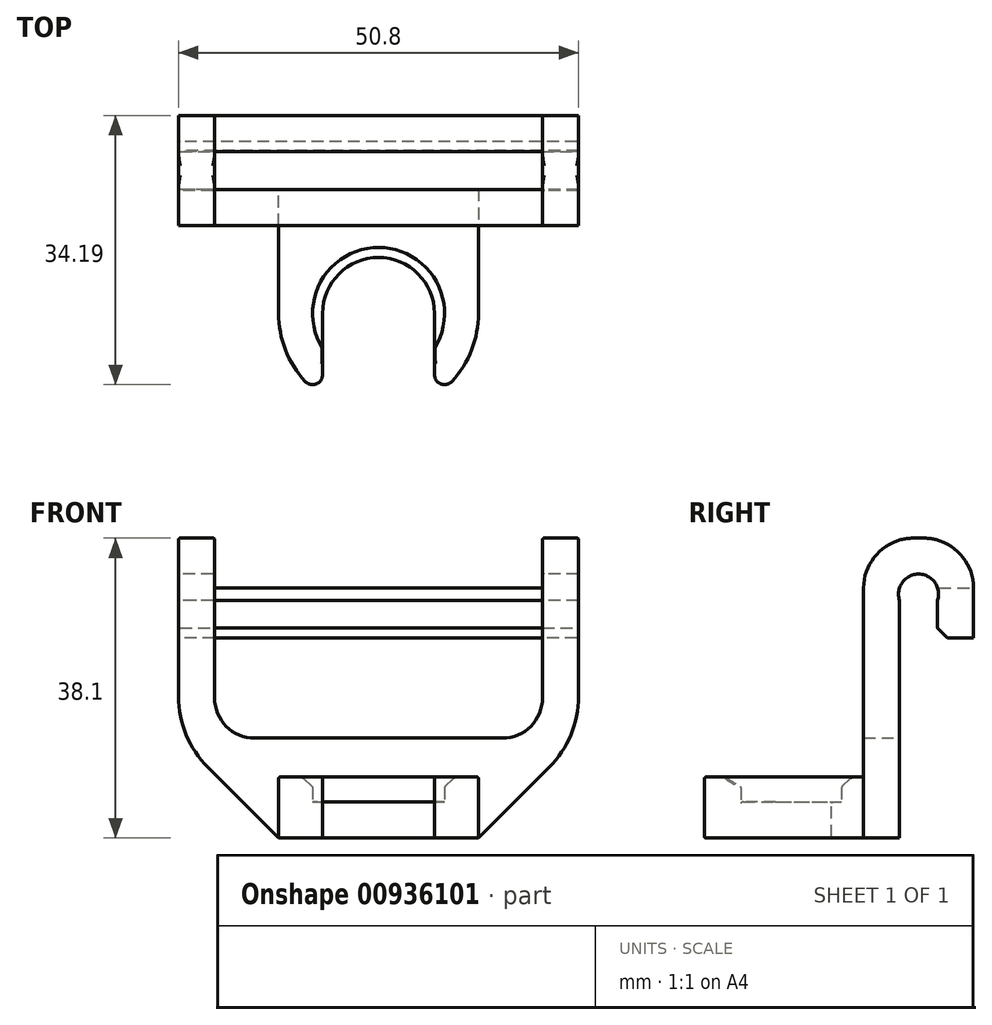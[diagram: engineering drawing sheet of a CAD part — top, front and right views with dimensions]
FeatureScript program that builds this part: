
annotation { "Feature Type Name" : "Feature", "Feature Type Description" : "" }
export const myFeature = defineFeature(function(context is Context, id is Id, definition is map)
    precondition{}
    {
        {
            var Q0;
            Q0=qCreatedBy(makeId("Top.planeOp"),FACE);
            var sketch = newSketch(context, id + "F0", { "sketchPlane" : qUnion([Q0])});
            skArc(sketch, "E0", {"start": v(-12.7, 0) * mm, "mid": v(0, -12.7) * mm, "end": v(12.7, 0) * mm});
            skLineSegment(sketch, "E1.top", {"start": v(-12.7, 11.18) * mm, "end": v(12.7, 11.18) * mm});
            skLineSegment(sketch, "E1.left", {"start": v(-12.7, 0) * mm, "end": v(-12.7, 11.18) * mm});
            skLineSegment(sketch, "E1.right", {"start": v(12.7, 0) * mm, "end": v(12.7, 11.18) * mm});
            skLineSegment(sketch, "E2", {"start": v(-12.7, 0) * mm, "end": v(12.7, 0) * mm, "construction": true});
            skSolve(sketch);
        }
        {
            var Q0;
            Q0=makeQuery(id+"F0.imprint","IMPRINT",FACE,{"disambiguationData":[TD([[makeQuery(id+"F0.imprint","IMPRINT",EDGE,{"derivedFrom":sQuery(id+"F0.wireOp",EDGE,"E0")}),1.0]])]});
            extrude(context, id + "F1", {"entities" : qUnion([Q0]), "depth" : 4.57 * mm, "offsetDistance" : 25.4 * mm});
        }
        {
            var Q0;
            Q0=makeQuery(id+"F1.opExtrude","CAP_FACE",FACE,{"disambiguationData":[OSD([sQuery(id+"F0.wireOp",EDGE,"E0"),sQuery(id+"F0.wireOp",EDGE,"E1.top"),sQuery(id+"F0.wireOp",EDGE,"E1.left"),sQuery(id+"F0.wireOp",EDGE,"E1.right")])],"isStart":false});
            var sketch = newSketch(context, id + "F2", { "sketchPlane" : qUnion([Q0])});
            skCircle(sketch, "E3", {"center": v(0, 0) * mm, "radius": 8.38 * mm});
            skArc(sketch, "E4", {"start": v(-12.7, 0) * mm, "mid": v(0, -12.7) * mm, "end": v(12.7, 0) * mm});
            skLineSegment(sketch, "E5.bottom", {"start": v(-12.7, 11.18) * mm, "end": v(12.7, 11.18) * mm});
            skLineSegment(sketch, "E5.left", {"start": v(-12.7, 11.18) * mm, "end": v(-12.7, 0) * mm});
            skLineSegment(sketch, "E5.right", {"start": v(12.7, 11.18) * mm, "end": v(12.7, 0) * mm});
            skSolve(sketch);
        }
        {
            var Q0;
            Q0 = qSketchRegion(id + "F2", true);
            extrude(context, id + "F3", {"entities" : qUnion([Q0]), "operationType" : NewBodyOperationType.ADD, "depth" : 3.17 * mm, "offsetDistance" : 25.4 * mm});
        }
        {
            var Q0;
            Q0=makeQuery(id+"F1.opExtrude","CAP_FACE",FACE,{"disambiguationData":[OSD([sQuery(id+"F0.wireOp",EDGE,"E0"),sQuery(id+"F0.wireOp",EDGE,"E1.top"),sQuery(id+"F0.wireOp",EDGE,"E1.left"),sQuery(id+"F0.wireOp",EDGE,"E1.right")])],"isStart":false});
            var sketch = newSketch(context, id + "F4", { "sketchPlane" : qUnion([Q0])});
            skArc(sketch, "E6", {"start": v(7.11, 0) * mm, "mid": v(0, 7.11) * mm, "end": v(-7.11, 0) * mm});
            skLineSegment(sketch, "E7.top", {"start": v(-7.11, -29.61) * mm, "end": v(7.11, -29.61) * mm});
            skLineSegment(sketch, "E7.left", {"start": v(-7.11, 0) * mm, "end": v(-7.11, -29.61) * mm});
            skLineSegment(sketch, "E7.right", {"start": v(7.11, 0) * mm, "end": v(7.11, -29.61) * mm});
            skLineSegment(sketch, "E8", {"start": v(-7.11, 0) * mm, "end": v(7.11, 0) * mm, "construction": true});
            skSolve(sketch);
        }
        {
            var Q0;
            Q0 = qSketchRegion(id + "F4", true);
            extrude(context, id + "F5", {"entities" : qUnion([Q0]), "operationType" : NewBodyOperationType.REMOVE, "oppositeDirection" : true, "depth" : 25.4 * mm, "offsetDistance" : 25.4 * mm, "symmetric" : true});
        }
        {
            var Q0;
            Q0=makeQuery(id+"F5.boolean.opBoolean","INTERSECT",EDGE,{"derivedFrom":[makeQuery(id+"F3.boolean.opBoolean","MERGE",FACE,{"derivedFrom":[makeQuery(id+"F1.opExtrude","SWEPT_FACE",FACE,{"disambiguationData":[OSD([sQuery(id+"F0.wireOp",EDGE,"E0")])]}),makeQuery(id+"F3.opExtrude","SWEPT_FACE",FACE,{"disambiguationData":[OSD([sQuery(id+"F2.wireOp",EDGE,"E4")])]})]}),makeQuery(id+"F5.opExtrude","SWEPT_FACE",FACE,{"disambiguationData":[OSD([sQuery(id+"F4.wireOp",EDGE,"E7.left")])]})]});
            var Q1;
            Q1=makeQuery(id+"F5.boolean.opBoolean","INTERSECT",EDGE,{"derivedFrom":[makeQuery(id+"F3.boolean.opBoolean","MERGE",FACE,{"derivedFrom":[makeQuery(id+"F1.opExtrude","SWEPT_FACE",FACE,{"disambiguationData":[OSD([sQuery(id+"F0.wireOp",EDGE,"E0")])]}),makeQuery(id+"F3.opExtrude","SWEPT_FACE",FACE,{"disambiguationData":[OSD([sQuery(id+"F2.wireOp",EDGE,"E4")])]})]}),makeQuery(id+"F5.opExtrude","SWEPT_FACE",FACE,{"disambiguationData":[OSD([sQuery(id+"F4.wireOp",EDGE,"E7.right")])]})]});
            fillet(context, id + "F6", {"entities" : qUnion([Q0, Q1]), "radius" : 1.27 * mm, "tangentPropagation" : true, "allowEdgeOverflow" : false});
        }
        {
            var Q0;
            Q0=makeQuery(id+"F3.opExtrude","CAP_EDGE",EDGE,{"disambiguationData":[OSD([sQuery(id+"F2.wireOp",EDGE,"E3")])],"isStart":false});
            chamfer(context, id + "F7", {"entities" : qUnion([Q0]), "width" : 1.27 * mm});
        }
        {
            var Q0;
            Q0=qCreatedBy(makeId("Right.planeOp"),FACE);
            var sketch = newSketch(context, id + "F8", { "sketchPlane" : qUnion([Q0])});
            skLineSegment(sketch, "E9.bottom", {"start": v(25.15, 0) * mm, "end": v(11.18, 0) * mm});
            skLineSegment(sketch, "E9.top", {"start": v(25.15, 38.1) * mm, "end": v(11.18, 38.1) * mm});
            skLineSegment(sketch, "E9.left", {"start": v(11.18, 0) * mm, "end": v(11.18, 38.1) * mm});
            skLineSegment(sketch, "E9.right", {"start": v(25.15, 0) * mm, "end": v(25.15, 38.1) * mm});
            skSolve(sketch);
        }
        {
            var Q0;
            Q0 = qSketchRegion(id + "F8", true);
            extrude(context, id + "F9", {"entities" : qUnion([Q0]), "operationType" : NewBodyOperationType.ADD, "depth" : 50.8 * mm, "offsetDistance" : 25.4 * mm, "symmetric" : true});
        }
        {
            var Q0;
            Q0=makeQuery(id+"F9.opExtrude","CAP_EDGE",EDGE,{"disambiguationData":[OSD([sQuery(id+"F8.wireOp",EDGE,"E9.bottom")])],"isStart":false});
            var Q1;
            Q1=makeQuery(id+"F9.opExtrude","CAP_EDGE",EDGE,{"disambiguationData":[OSD([sQuery(id+"F8.wireOp",EDGE,"E9.bottom")])],"isStart":true});
            chamfer(context, id + "F10", {"entities" : qUnion([Q0, Q1]), "width" : 12.7 * mm, "tangentPropagation" : true});
        }
        {
            var Q0;
            Q0=makeQuery(id+"F9.opExtrude","CAP_FACE",FACE,{"disambiguationData":[OSD([sQuery(id+"F8.wireOp",EDGE,"E9.bottom"),sQuery(id+"F8.wireOp",EDGE,"E9.top"),sQuery(id+"F8.wireOp",EDGE,"E9.left"),sQuery(id+"F8.wireOp",EDGE,"E9.right")])],"isStart":true});
            var sketch = newSketch(context, id + "F11", { "sketchPlane" : qUnion([Q0])});
            skLineSegment(sketch, "E10", {"start": v(-18.16, 38.1) * mm, "end": v(-18.16, 12.7) * mm, "construction": true});
            skArc(sketch, "E11", {"start": v(-15.75, 30.2) * mm, "mid": v(-18.16, 33.53) * mm, "end": v(-20.57, 30.2) * mm});
            skPoint(sketch, "E12", {"position": v(-18.16, 33.53) * mm});
            skLineSegment(sketch, "E13.left", {"start": v(-20.57, 30.2) * mm, "end": v(-20.57, 25.4) * mm});
            skLineSegment(sketch, "E13.right", {"start": v(-15.75, 30.2) * mm, "end": v(-15.75, 0) * mm});
            skPoint(sketch, "E13.middle", {"position": v(-18.16, 15.1) * mm});
            skLineSegment(sketch, "E14.bottom", {"start": v(-20.57, 25.4) * mm, "end": v(-25.15, 25.4) * mm});
            skLineSegment(sketch, "E14.top", {"start": v(-15.75, 0) * mm, "end": v(-25.15, 0) * mm});
            skLineSegment(sketch, "E14.right", {"start": v(-25.15, 25.4) * mm, "end": v(-25.15, 0) * mm});
            skPoint(sketch, "E13.top.start.orphan", {"position": v(-20.57, 0) * mm});
            skSolve(sketch);
        }
        {
            var Q0;
            Q0 = qSketchRegion(id + "F11", true);
            var Q1;
            Q1=makeQuery(id+"F9.opExtrude","CAP_FACE",FACE,{"disambiguationData":[OSD([sQuery(id+"F8.wireOp",EDGE,"E9.bottom"),sQuery(id+"F8.wireOp",EDGE,"E9.top"),sQuery(id+"F8.wireOp",EDGE,"E9.left"),sQuery(id+"F8.wireOp",EDGE,"E9.right")])],"isStart":false});
            extrude(context, id + "F12", {"entities" : qUnion([Q0]), "operationType" : NewBodyOperationType.REMOVE, "endBound" : BoundingType.UP_TO_SURFACE, "oppositeDirection" : true, "depth" : 25.4 * mm, "endBoundEntityFace" : qUnion([Q1]), "offsetDistance" : 25.4 * mm});
        }
        {
            var Q0;
            Q0=makeQuery(id+"F12.boolean.opBoolean","COPY",EDGE,{"derivedFrom":makeQuery(id+"F12.opExtrude","SWEPT_EDGE",EDGE,{"disambiguationData":[OSD([sQuery(id+"F11.wireOp",EDGE,"E13.left"),sQuery(id+"F11.wireOp",EDGE,"E14.bottom")])]})});
            chamfer(context, id + "F13", {"entities" : qUnion([Q0]), "width" : 1.27 * mm, "tangentPropagation" : true});
        }
        {
            var Q0;
            Q0=makeQuery(id+"F9.opExtrude","SWEPT_EDGE",EDGE,{"disambiguationData":[OSD([sQuery(id+"F8.wireOp",EDGE,"E9.top"),sQuery(id+"F8.wireOp",EDGE,"E9.left")])]});
            var Q1;
            Q1=makeQuery(id+"F9.opExtrude","SWEPT_EDGE",EDGE,{"disambiguationData":[OSD([sQuery(id+"F8.wireOp",EDGE,"E9.top"),sQuery(id+"F8.wireOp",EDGE,"E9.right")])]});
            fillet(context, id + "F14", {"entities" : qUnion([Q0, Q1]), "radius" : 6.35 * mm, "tangentPropagation" : true, "allowEdgeOverflow" : false});
        }
        {
            var Q0;
            {var subQ0=sQuery(id+"F8.wireOp",EDGE,"E9.bottom");Q0=makeQuery(id+"F10.opChamfer","BLEND_EDGE",EDGE,{"blendedFrom":[makeQuery(id+"F9.opExtrude","CAP_EDGE",EDGE,{"disambiguationData":[OSD([subQ0])],"isStart":true}),makeQuery(id+"F9.opExtrude","CAP_FACE",FACE,{"disambiguationData":[OSD([subQ0,sQuery(id+"F8.wireOp",EDGE,"E9.top"),sQuery(id+"F8.wireOp",EDGE,"E9.left"),sQuery(id+"F8.wireOp",EDGE,"E9.right")])],"isStart":true})],"blendedInto":[makeQuery(id+"F9.opExtrude","CAP_FACE",FACE,{"disambiguationData":[OSD([subQ0,sQuery(id+"F8.wireOp",EDGE,"E9.top"),sQuery(id+"F8.wireOp",EDGE,"E9.left"),sQuery(id+"F8.wireOp",EDGE,"E9.right")])],"isStart":true})]});}
            var Q1;
            {var subQ0=sQuery(id+"F8.wireOp",EDGE,"E9.bottom");Q1=makeQuery(id+"F10.opChamfer","BLEND_EDGE",EDGE,{"blendedFrom":[makeQuery(id+"F9.opExtrude","CAP_EDGE",EDGE,{"disambiguationData":[OSD([subQ0])],"isStart":false}),makeQuery(id+"F9.opExtrude","CAP_FACE",FACE,{"disambiguationData":[OSD([subQ0,sQuery(id+"F8.wireOp",EDGE,"E9.top"),sQuery(id+"F8.wireOp",EDGE,"E9.left"),sQuery(id+"F8.wireOp",EDGE,"E9.right")])],"isStart":false})],"blendedInto":[makeQuery(id+"F9.opExtrude","CAP_FACE",FACE,{"disambiguationData":[OSD([subQ0,sQuery(id+"F8.wireOp",EDGE,"E9.top"),sQuery(id+"F8.wireOp",EDGE,"E9.left"),sQuery(id+"F8.wireOp",EDGE,"E9.right")])],"isStart":false})]});}
            fillet(context, id + "F15", {"entities" : qUnion([Q0, Q1]), "radius" : 12.7 * mm, "tangentPropagation" : true, "allowEdgeOverflow" : false});
        }
        {
            var Q0;
            Q0=makeQuery(id+"F9.opExtrude","SWEPT_FACE",FACE,{"disambiguationData":[OSD([sQuery(id+"F8.wireOp",EDGE,"E9.right")])]});
            var sketch = newSketch(context, id + "F16", { "sketchPlane" : qUnion([Q0])});
            skLineSegment(sketch, "E15.bottom", {"start": v(20.83, 31.75) * mm, "end": v(-20.83, 31.75) * mm});
            skLineSegment(sketch, "E15.top", {"start": v(20.83, 44.33) * mm, "end": v(-20.83, 44.33) * mm});
            skLineSegment(sketch, "E15.left", {"start": v(20.83, 31.75) * mm, "end": v(20.83, 44.33) * mm});
            skLineSegment(sketch, "E15.right", {"start": v(-20.83, 31.75) * mm, "end": v(-20.83, 44.33) * mm});
            skPoint(sketch, "E15.middle", {"position": v(0, 38.04) * mm});
            skPoint(sketch, "E15.middle.positionSnap0", {"position": v(0, 31.75) * mm});
            skPoint(sketch, "E15.centerSnap0", {"position": v(0, 31.75) * mm});
            skSolve(sketch);
        }
        {
            var Q0;
            Q0 = qSketchRegion(id + "F16", true);
            extrude(context, id + "F17", {"entities" : qUnion([Q0]), "operationType" : NewBodyOperationType.REMOVE, "oppositeDirection" : true, "depth" : 25.4 * mm, "offsetDistance" : 25.4 * mm});
        }
        {
            var Q0;
            {var subQ0=sQuery(id+"F8.wireOp",EDGE,"E9.left");Q0=makeQuery(id+"F17.boolean.opBoolean","COPY",FACE,{"disambiguationData":[TD([makeQuery(id+"F9.opExtrude","SWEPT_FACE",FACE,{"disambiguationData":[OSD([subQ0])]})])],"derivedFrom":makeQuery(id+"F17.opExtrude","SWEPT_FACE",FACE,{"disambiguationData":[OSD([sQuery(id+"F16.wireOp",EDGE,"E15.bottom")])]})});}
            extrude(context, id + "F18", {"entities" : qUnion([Q0]), "operationType" : NewBodyOperationType.REMOVE, "oppositeDirection" : true, "depth" : 19.05 * mm, "offsetDistance" : 25.4 * mm});
        }
        {
            var Q0;
            Q0=makeQuery(id+"F18.boolean.opBoolean","COPY",FACE,{"derivedFrom":makeQuery(id+"F18.opExtrude","SWEPT_FACE",FACE,{"disambiguationData":[OSD([sQuery(id+"F11.wireOp",EDGE,"E11"),sQuery(id+"F16.wireOp",EDGE,"E15.bottom")])]})});
            extrude(context, id + "F19", {"entities" : qUnion([Q0]), "operationType" : NewBodyOperationType.REMOVE, "oppositeDirection" : true, "depth" : 0.5 * mm, "offsetDistance" : 25.4 * mm});
        }
        {
            var Q0;
            {var subQ0=sQuery(id+"F16.wireOp",EDGE,"E15.left");var subQ1=sQuery(id+"F16.wireOp",EDGE,"E15.bottom");Q0=makeQuery(id+"F19.boolean.opBoolean","MERGE",EDGE,{"derivedFrom":[makeQuery(id+"F18.boolean.opBoolean","COPY",EDGE,{"derivedFrom":makeQuery(id+"F18.opExtrude","CAP_EDGE",EDGE,{"disambiguationData":[OSD([sQuery(id+"F8.wireOp",EDGE,"E9.top"),sQuery(id+"F8.wireOp",EDGE,"E9.right"),subQ1,subQ0])],"isStart":false})})],"fromTools":[makeQuery(id+"F19.opExtrude","SWEPT_EDGE",EDGE,{"disambiguationData":[OSD([sQuery(id+"F11.wireOp",EDGE,"E11"),subQ1,subQ0])]})]});}
            var Q1;
            {var subQ0=sQuery(id+"F16.wireOp",EDGE,"E15.right");var subQ1=sQuery(id+"F16.wireOp",EDGE,"E15.bottom");Q1=makeQuery(id+"F19.boolean.opBoolean","MERGE",EDGE,{"derivedFrom":[makeQuery(id+"F18.boolean.opBoolean","COPY",EDGE,{"derivedFrom":makeQuery(id+"F18.opExtrude","CAP_EDGE",EDGE,{"disambiguationData":[OSD([sQuery(id+"F8.wireOp",EDGE,"E9.top"),sQuery(id+"F8.wireOp",EDGE,"E9.right"),subQ1,subQ0])],"isStart":false})})],"fromTools":[makeQuery(id+"F19.opExtrude","SWEPT_EDGE",EDGE,{"disambiguationData":[OSD([sQuery(id+"F11.wireOp",EDGE,"E11"),subQ1,subQ0])]})]});}
            fillet(context, id + "F20", {"entities" : qUnion([Q0, Q1]), "radius" : 5.08 * mm, "tangentPropagation" : true, "allowEdgeOverflow" : false});
        }
        {
            var Q0;
            Q0=makeQuery(id+"F1.opExtrude","CAP_EDGE",EDGE,{"disambiguationData":[OSD([sQuery(id+"F0.wireOp",EDGE,"E1.right")])],"isStart":true});
            var Q1;
            Q1=makeQuery(id+"F12.boolean.opBoolean","COPY",EDGE,{"derivedFrom":makeQuery(id+"F12.opExtrude","CAP_EDGE",EDGE,{"disambiguationData":[OSD([sQuery(id+"F11.wireOp",EDGE,"E14.bottom")])],"isStart":false})});
            var Q2;
            Q2=makeQuery(id+"F13.opChamfer","BLEND_EDGE",EDGE,{"blendedFrom":[makeQuery(id+"F12.boolean.opBoolean","COPY",EDGE,{"derivedFrom":makeQuery(id+"F12.opExtrude","SWEPT_EDGE",EDGE,{"disambiguationData":[OSD([sQuery(id+"F11.wireOp",EDGE,"E13.left"),sQuery(id+"F11.wireOp",EDGE,"E14.bottom")])]})}),makeQuery(id+"F9.opExtrude","CAP_FACE",FACE,{"disambiguationData":[OSD([sQuery(id+"F8.wireOp",EDGE,"E9.bottom"),sQuery(id+"F8.wireOp",EDGE,"E9.top"),sQuery(id+"F8.wireOp",EDGE,"E9.left"),sQuery(id+"F8.wireOp",EDGE,"E9.right")])],"isStart":false})],"blendedInto":[makeQuery(id+"F9.opExtrude","CAP_FACE",FACE,{"disambiguationData":[OSD([sQuery(id+"F8.wireOp",EDGE,"E9.bottom"),sQuery(id+"F8.wireOp",EDGE,"E9.top"),sQuery(id+"F8.wireOp",EDGE,"E9.left"),sQuery(id+"F8.wireOp",EDGE,"E9.right")])],"isStart":false})]});
            var Q3;
            Q3=makeQuery(id+"F12.boolean.opBoolean","COPY",EDGE,{"derivedFrom":makeQuery(id+"F12.opExtrude","CAP_EDGE",EDGE,{"disambiguationData":[OSD([sQuery(id+"F11.wireOp",EDGE,"E11")])],"isStart":false})});
            var Q4;
            {var subQ0=sQuery(id+"F11.wireOp",EDGE,"E11");Q4=makeQuery(id+"F19.boolean.opBoolean","INTERSECT",EDGE,{"derivedFrom":[makeQuery(id+"F12.boolean.opBoolean","COPY",FACE,{"derivedFrom":makeQuery(id+"F12.opExtrude","SWEPT_FACE",FACE,{"disambiguationData":[OSD([subQ0])]})}),makeQuery(id+"F19.opExtrude","SWEPT_FACE",FACE,{"disambiguationData":[OSD([subQ0,sQuery(id+"F16.wireOp",EDGE,"E15.bottom"),sQuery(id+"F16.wireOp",EDGE,"E15.right")])]})]});}
            var Q5;
            {var subQ0=sQuery(id+"F11.wireOp",EDGE,"E11");Q5=makeQuery(id+"F19.boolean.opBoolean","INTERSECT",EDGE,{"derivedFrom":[makeQuery(id+"F12.boolean.opBoolean","COPY",FACE,{"derivedFrom":makeQuery(id+"F12.opExtrude","SWEPT_FACE",FACE,{"disambiguationData":[OSD([subQ0])]})}),makeQuery(id+"F19.opExtrude","SWEPT_FACE",FACE,{"disambiguationData":[OSD([subQ0,sQuery(id+"F16.wireOp",EDGE,"E15.bottom"),sQuery(id+"F16.wireOp",EDGE,"E15.left")])]})]});}
            var Q6;
            Q6=makeQuery(id+"F12.boolean.opBoolean","COPY",EDGE,{"derivedFrom":makeQuery(id+"F12.opExtrude","CAP_EDGE",EDGE,{"disambiguationData":[OSD([sQuery(id+"F11.wireOp",EDGE,"E14.bottom")])],"isStart":true})});
            var Q7;
            Q7=makeQuery(id+"F13.opChamfer","BLEND_EDGE",EDGE,{"blendedFrom":[makeQuery(id+"F12.boolean.opBoolean","COPY",EDGE,{"derivedFrom":makeQuery(id+"F12.opExtrude","SWEPT_EDGE",EDGE,{"disambiguationData":[OSD([sQuery(id+"F11.wireOp",EDGE,"E13.left"),sQuery(id+"F11.wireOp",EDGE,"E14.bottom")])]})}),makeQuery(id+"F9.opExtrude","CAP_FACE",FACE,{"disambiguationData":[OSD([sQuery(id+"F8.wireOp",EDGE,"E9.bottom"),sQuery(id+"F8.wireOp",EDGE,"E9.top"),sQuery(id+"F8.wireOp",EDGE,"E9.left"),sQuery(id+"F8.wireOp",EDGE,"E9.right")])],"isStart":true})],"blendedInto":[makeQuery(id+"F9.opExtrude","CAP_FACE",FACE,{"disambiguationData":[OSD([sQuery(id+"F8.wireOp",EDGE,"E9.bottom"),sQuery(id+"F8.wireOp",EDGE,"E9.top"),sQuery(id+"F8.wireOp",EDGE,"E9.left"),sQuery(id+"F8.wireOp",EDGE,"E9.right")])],"isStart":true})]});
            var Q8;
            Q8=makeQuery(id+"F1.opExtrude","CAP_EDGE",EDGE,{"disambiguationData":[OSD([sQuery(id+"F0.wireOp",EDGE,"E1.left")])],"isStart":true});
            var Q9;
            {var subQ0=sQuery(id+"F0.wireOp",EDGE,"E1.left");var subQ1=sQuery(id+"F0.wireOp",EDGE,"E0");Q9=makeQuery(id+"F5.boolean.opBoolean","SPLIT",EDGE,{"disambiguationData":[TD([makeQuery(id+"F1.opExtrude","SWEPT_FACE",FACE,{"disambiguationData":[OSD([subQ0])]})])],"derivedFrom":makeQuery(id+"F1.opExtrude","CAP_EDGE",EDGE,{"disambiguationData":[OSD([subQ1])],"isStart":true})});}
            var Q10;
            Q10=makeQuery(id+"F5.boolean.opBoolean","INTERSECT",EDGE,{"derivedFrom":[makeQuery(id+"F1.opExtrude","CAP_FACE",FACE,{"disambiguationData":[OSD([sQuery(id+"F0.wireOp",EDGE,"E0"),sQuery(id+"F0.wireOp",EDGE,"E1.top"),sQuery(id+"F0.wireOp",EDGE,"E1.left"),sQuery(id+"F0.wireOp",EDGE,"E1.right")])],"isStart":true}),makeQuery(id+"F5.opExtrude","SWEPT_FACE",FACE,{"disambiguationData":[OSD([sQuery(id+"F4.wireOp",EDGE,"E6")])]})]});
            var Q11;
            Q11=makeQuery(id+"F5.boolean.opBoolean","INTERSECT",EDGE,{"derivedFrom":[makeQuery(id+"F1.opExtrude","CAP_FACE",FACE,{"disambiguationData":[OSD([sQuery(id+"F0.wireOp",EDGE,"E0"),sQuery(id+"F0.wireOp",EDGE,"E1.top"),sQuery(id+"F0.wireOp",EDGE,"E1.left"),sQuery(id+"F0.wireOp",EDGE,"E1.right")])],"isStart":true}),makeQuery(id+"F5.opExtrude","SWEPT_FACE",FACE,{"disambiguationData":[OSD([sQuery(id+"F4.wireOp",EDGE,"E7.right")])]})]});
            var Q12;
            Q12=makeQuery(id+"F5.boolean.opBoolean","INTERSECT",EDGE,{"derivedFrom":[makeQuery(id+"F1.opExtrude","CAP_FACE",FACE,{"disambiguationData":[OSD([sQuery(id+"F0.wireOp",EDGE,"E0"),sQuery(id+"F0.wireOp",EDGE,"E1.top"),sQuery(id+"F0.wireOp",EDGE,"E1.left"),sQuery(id+"F0.wireOp",EDGE,"E1.right")])],"isStart":true}),makeQuery(id+"F5.opExtrude","SWEPT_FACE",FACE,{"disambiguationData":[OSD([sQuery(id+"F4.wireOp",EDGE,"E7.left")])]})]});
            var Q13;
            Q13=makeQuery(id+"F3.opExtrude","CAP_EDGE",EDGE,{"disambiguationData":[OSD([sQuery(id+"F2.wireOp",EDGE,"E5.left")])],"isStart":false});
            var Q14;
            Q14=makeQuery(id+"F3.opExtrude","CAP_EDGE",EDGE,{"disambiguationData":[OSD([sQuery(id+"F2.wireOp",EDGE,"E5.right")])],"isStart":false});
            var Q15;
            {var subQ0=sQuery(id+"F2.wireOp",EDGE,"E3");Q15=makeQuery(id+"F7.opChamfer","BLEND_EDGE",EDGE,{"blendedFrom":[makeQuery(id+"F3.opExtrude","CAP_EDGE",EDGE,{"disambiguationData":[OSD([subQ0])],"isStart":false}),makeQuery(id+"F3.opExtrude","SWEPT_FACE",FACE,{"disambiguationData":[OSD([subQ0])]})],"blendedInto":[makeQuery(id+"F3.opExtrude","SWEPT_FACE",FACE,{"disambiguationData":[OSD([subQ0])]})]});}
            var Q16;
            Q16=makeQuery(id+"F5.boolean.opBoolean","INTERSECT",EDGE,{"derivedFrom":[makeQuery(id+"F1.opExtrude","CAP_FACE",FACE,{"disambiguationData":[OSD([sQuery(id+"F0.wireOp",EDGE,"E0"),sQuery(id+"F0.wireOp",EDGE,"E1.top"),sQuery(id+"F0.wireOp",EDGE,"E1.left"),sQuery(id+"F0.wireOp",EDGE,"E1.right")])],"isStart":false}),makeQuery(id+"F5.opExtrude","SWEPT_FACE",FACE,{"disambiguationData":[OSD([sQuery(id+"F4.wireOp",EDGE,"E6")])]})]});
            var Q17;
            Q17=makeQuery(id+"F9.opExtrude","CAP_EDGE",EDGE,{"disambiguationData":[OSD([sQuery(id+"F8.wireOp",EDGE,"E9.top")])],"isStart":false});
            var Q18;
            Q18=makeQuery(id+"F17.boolean.opBoolean","INTERSECT",EDGE,{"derivedFrom":[makeQuery(id+"F9.opExtrude","SWEPT_FACE",FACE,{"disambiguationData":[OSD([sQuery(id+"F8.wireOp",EDGE,"E9.top")])]}),makeQuery(id+"F17.opExtrude","SWEPT_FACE",FACE,{"disambiguationData":[OSD([sQuery(id+"F16.wireOp",EDGE,"E15.right")])]})]});
            var Q19;
            Q19=makeQuery(id+"F17.boolean.opBoolean","INTERSECT",EDGE,{"derivedFrom":[makeQuery(id+"F9.opExtrude","SWEPT_FACE",FACE,{"disambiguationData":[OSD([sQuery(id+"F8.wireOp",EDGE,"E9.top")])]}),makeQuery(id+"F17.opExtrude","SWEPT_FACE",FACE,{"disambiguationData":[OSD([sQuery(id+"F16.wireOp",EDGE,"E15.left")])]})]});
            var Q20;
            Q20=makeQuery(id+"F9.opExtrude","CAP_EDGE",EDGE,{"disambiguationData":[OSD([sQuery(id+"F8.wireOp",EDGE,"E9.top")])],"isStart":true});
            var Q21;
            {var subQ0=sQuery(id+"F2.wireOp",EDGE,"E3");Q21=makeQuery(id+"F7.opChamfer","BLEND_EDGE",EDGE,{"blendedFrom":[makeQuery(id+"F3.opExtrude","CAP_EDGE",EDGE,{"disambiguationData":[OSD([subQ0])],"isStart":false}),makeQuery(id+"F3.opExtrude","CAP_FACE",FACE,{"disambiguationData":[OSD([subQ0,sQuery(id+"F2.wireOp",EDGE,"E4"),sQuery(id+"F2.wireOp",EDGE,"E5.bottom"),sQuery(id+"F2.wireOp",EDGE,"E5.left"),sQuery(id+"F2.wireOp",EDGE,"E5.right")])],"isStart":false})],"blendedInto":[makeQuery(id+"F3.opExtrude","CAP_FACE",FACE,{"disambiguationData":[OSD([subQ0,sQuery(id+"F2.wireOp",EDGE,"E4"),sQuery(id+"F2.wireOp",EDGE,"E5.bottom"),sQuery(id+"F2.wireOp",EDGE,"E5.left"),sQuery(id+"F2.wireOp",EDGE,"E5.right")])],"isStart":false})]});}
            var Q22;
            Q22=makeQuery(id+"F5.boolean.opBoolean","INTERSECT",EDGE,{"derivedFrom":[makeQuery(id+"F1.opExtrude","CAP_FACE",FACE,{"disambiguationData":[OSD([sQuery(id+"F0.wireOp",EDGE,"E0"),sQuery(id+"F0.wireOp",EDGE,"E1.top"),sQuery(id+"F0.wireOp",EDGE,"E1.left"),sQuery(id+"F0.wireOp",EDGE,"E1.right")])],"isStart":false}),makeQuery(id+"F5.opExtrude","SWEPT_FACE",FACE,{"disambiguationData":[OSD([sQuery(id+"F4.wireOp",EDGE,"E7.left")])]})]});
            var Q23;
            Q23=makeQuery(id+"F5.boolean.opBoolean","INTERSECT",EDGE,{"derivedFrom":[makeQuery(id+"F1.opExtrude","CAP_FACE",FACE,{"disambiguationData":[OSD([sQuery(id+"F0.wireOp",EDGE,"E0"),sQuery(id+"F0.wireOp",EDGE,"E1.top"),sQuery(id+"F0.wireOp",EDGE,"E1.left"),sQuery(id+"F0.wireOp",EDGE,"E1.right")])],"isStart":false}),makeQuery(id+"F5.opExtrude","SWEPT_FACE",FACE,{"disambiguationData":[OSD([sQuery(id+"F4.wireOp",EDGE,"E7.right")])]})]});
            var Q24;
            Q24=makeQuery(id+"F7.opChamfer","BLEND_EDGE",EDGE,{"blendedFrom":[makeQuery(id+"F3.opExtrude","CAP_EDGE",EDGE,{"disambiguationData":[OSD([sQuery(id+"F2.wireOp",EDGE,"E3")])],"isStart":false}),makeQuery(id+"F5.boolean.opBoolean","COPY",FACE,{"derivedFrom":makeQuery(id+"F5.opExtrude","SWEPT_FACE",FACE,{"disambiguationData":[OSD([sQuery(id+"F4.wireOp",EDGE,"E7.right")])]})})],"blendedInto":[makeQuery(id+"F5.boolean.opBoolean","COPY",FACE,{"derivedFrom":makeQuery(id+"F5.opExtrude","SWEPT_FACE",FACE,{"disambiguationData":[OSD([sQuery(id+"F4.wireOp",EDGE,"E7.right")])]})})]});
            var Q25;
            Q25=makeQuery(id+"F7.opChamfer","BLEND_EDGE",EDGE,{"blendedFrom":[makeQuery(id+"F3.opExtrude","CAP_EDGE",EDGE,{"disambiguationData":[OSD([sQuery(id+"F2.wireOp",EDGE,"E3")])],"isStart":false}),makeQuery(id+"F5.boolean.opBoolean","COPY",FACE,{"derivedFrom":makeQuery(id+"F5.opExtrude","SWEPT_FACE",FACE,{"disambiguationData":[OSD([sQuery(id+"F4.wireOp",EDGE,"E7.left")])]})})],"blendedInto":[makeQuery(id+"F5.boolean.opBoolean","COPY",FACE,{"derivedFrom":makeQuery(id+"F5.opExtrude","SWEPT_FACE",FACE,{"disambiguationData":[OSD([sQuery(id+"F4.wireOp",EDGE,"E7.left")])]})})]});
            var Q26;
            Q26=makeQuery(id+"F5.boolean.opBoolean","INTERSECT",EDGE,{"derivedFrom":[makeQuery(id+"F3.opExtrude","CAP_FACE",FACE,{"disambiguationData":[OSD([sQuery(id+"F2.wireOp",EDGE,"E3"),sQuery(id+"F2.wireOp",EDGE,"E4"),sQuery(id+"F2.wireOp",EDGE,"E5.bottom"),sQuery(id+"F2.wireOp",EDGE,"E5.left"),sQuery(id+"F2.wireOp",EDGE,"E5.right")])],"isStart":false}),makeQuery(id+"F5.opExtrude","SWEPT_FACE",FACE,{"disambiguationData":[OSD([sQuery(id+"F4.wireOp",EDGE,"E7.left")])]})]});
            var Q27;
            Q27=makeQuery(id+"F5.boolean.opBoolean","INTERSECT",EDGE,{"derivedFrom":[makeQuery(id+"F3.opExtrude","CAP_FACE",FACE,{"disambiguationData":[OSD([sQuery(id+"F2.wireOp",EDGE,"E3"),sQuery(id+"F2.wireOp",EDGE,"E4"),sQuery(id+"F2.wireOp",EDGE,"E5.bottom"),sQuery(id+"F2.wireOp",EDGE,"E5.left"),sQuery(id+"F2.wireOp",EDGE,"E5.right")])],"isStart":false}),makeQuery(id+"F5.opExtrude","SWEPT_FACE",FACE,{"disambiguationData":[OSD([sQuery(id+"F4.wireOp",EDGE,"E7.right")])]})]});
            var Q28;
            {var subQ0=sQuery(id+"F2.wireOp",EDGE,"E4");Q28=makeQuery(id+"F5.boolean.opBoolean","SPLIT",EDGE,{"disambiguationData":[TD([makeQuery(id+"F1.opExtrude","SWEPT_FACE",FACE,{"disambiguationData":[OSD([sQuery(id+"F0.wireOp",EDGE,"E1.right")])]})])],"derivedFrom":makeQuery(id+"F3.opExtrude","CAP_EDGE",EDGE,{"disambiguationData":[OSD([subQ0])],"isStart":false})});}
            var Q29;
            {var subQ0=sQuery(id+"F2.wireOp",EDGE,"E4");Q29=makeQuery(id+"F5.boolean.opBoolean","SPLIT",EDGE,{"disambiguationData":[TD([makeQuery(id+"F1.opExtrude","SWEPT_FACE",FACE,{"disambiguationData":[OSD([sQuery(id+"F0.wireOp",EDGE,"E1.left")])]})])],"derivedFrom":makeQuery(id+"F3.opExtrude","CAP_EDGE",EDGE,{"disambiguationData":[OSD([subQ0])],"isStart":false})});}
            var Q30;
            {var subQ0=sQuery(id+"F2.wireOp",EDGE,"E4");Q30=makeQuery(id+"F6.opFillet","BLEND_EDGE",EDGE,{"blendedFrom":[makeQuery(id+"F5.boolean.opBoolean","INTERSECT",EDGE,{"derivedFrom":[makeQuery(id+"F3.boolean.opBoolean","MERGE",FACE,{"derivedFrom":[makeQuery(id+"F1.opExtrude","SWEPT_FACE",FACE,{"disambiguationData":[OSD([sQuery(id+"F0.wireOp",EDGE,"E0")])]}),makeQuery(id+"F3.opExtrude","SWEPT_FACE",FACE,{"disambiguationData":[OSD([subQ0])]})]}),makeQuery(id+"F5.opExtrude","SWEPT_FACE",FACE,{"disambiguationData":[OSD([sQuery(id+"F4.wireOp",EDGE,"E7.right")])]})]}),makeQuery(id+"F3.opExtrude","CAP_FACE",FACE,{"disambiguationData":[OSD([sQuery(id+"F2.wireOp",EDGE,"E3"),subQ0,sQuery(id+"F2.wireOp",EDGE,"E5.bottom"),sQuery(id+"F2.wireOp",EDGE,"E5.left"),sQuery(id+"F2.wireOp",EDGE,"E5.right")])],"isStart":false})],"blendedInto":[makeQuery(id+"F3.opExtrude","CAP_FACE",FACE,{"disambiguationData":[OSD([sQuery(id+"F2.wireOp",EDGE,"E3"),subQ0,sQuery(id+"F2.wireOp",EDGE,"E5.bottom"),sQuery(id+"F2.wireOp",EDGE,"E5.left"),sQuery(id+"F2.wireOp",EDGE,"E5.right")])],"isStart":false})]});}
            var Q31;
            {var subQ0=sQuery(id+"F2.wireOp",EDGE,"E4");Q31=makeQuery(id+"F6.opFillet","BLEND_EDGE",EDGE,{"blendedFrom":[makeQuery(id+"F5.boolean.opBoolean","INTERSECT",EDGE,{"derivedFrom":[makeQuery(id+"F3.boolean.opBoolean","MERGE",FACE,{"derivedFrom":[makeQuery(id+"F1.opExtrude","SWEPT_FACE",FACE,{"disambiguationData":[OSD([sQuery(id+"F0.wireOp",EDGE,"E0")])]}),makeQuery(id+"F3.opExtrude","SWEPT_FACE",FACE,{"disambiguationData":[OSD([subQ0])]})]}),makeQuery(id+"F5.opExtrude","SWEPT_FACE",FACE,{"disambiguationData":[OSD([sQuery(id+"F4.wireOp",EDGE,"E7.left")])]})]}),makeQuery(id+"F3.opExtrude","CAP_FACE",FACE,{"disambiguationData":[OSD([sQuery(id+"F2.wireOp",EDGE,"E3"),subQ0,sQuery(id+"F2.wireOp",EDGE,"E5.bottom"),sQuery(id+"F2.wireOp",EDGE,"E5.left"),sQuery(id+"F2.wireOp",EDGE,"E5.right")])],"isStart":false})],"blendedInto":[makeQuery(id+"F3.opExtrude","CAP_FACE",FACE,{"disambiguationData":[OSD([sQuery(id+"F2.wireOp",EDGE,"E3"),subQ0,sQuery(id+"F2.wireOp",EDGE,"E5.bottom"),sQuery(id+"F2.wireOp",EDGE,"E5.left"),sQuery(id+"F2.wireOp",EDGE,"E5.right")])],"isStart":false})]});}
            var Q32;
            {var subQ0=sQuery(id+"F0.wireOp",EDGE,"E1.right");var subQ1=sQuery(id+"F0.wireOp",EDGE,"E0");Q32=makeQuery(id+"F5.boolean.opBoolean","SPLIT",EDGE,{"disambiguationData":[TD([makeQuery(id+"F1.opExtrude","SWEPT_FACE",FACE,{"disambiguationData":[OSD([subQ0])]})])],"derivedFrom":makeQuery(id+"F1.opExtrude","CAP_EDGE",EDGE,{"disambiguationData":[OSD([subQ1])],"isStart":true})});}
            var Q33;
            {var subQ0=sQuery(id+"F0.wireOp",EDGE,"E0");Q33=makeQuery(id+"F6.opFillet","BLEND_EDGE",EDGE,{"blendedFrom":[makeQuery(id+"F5.boolean.opBoolean","INTERSECT",EDGE,{"derivedFrom":[makeQuery(id+"F3.boolean.opBoolean","MERGE",FACE,{"derivedFrom":[makeQuery(id+"F1.opExtrude","SWEPT_FACE",FACE,{"disambiguationData":[OSD([subQ0])]}),makeQuery(id+"F3.opExtrude","SWEPT_FACE",FACE,{"disambiguationData":[OSD([sQuery(id+"F2.wireOp",EDGE,"E4")])]})]}),makeQuery(id+"F5.opExtrude","SWEPT_FACE",FACE,{"disambiguationData":[OSD([sQuery(id+"F4.wireOp",EDGE,"E7.right")])]})]}),makeQuery(id+"F1.opExtrude","CAP_FACE",FACE,{"disambiguationData":[OSD([subQ0,sQuery(id+"F0.wireOp",EDGE,"E1.top"),sQuery(id+"F0.wireOp",EDGE,"E1.left"),sQuery(id+"F0.wireOp",EDGE,"E1.right")])],"isStart":true})],"blendedInto":[makeQuery(id+"F1.opExtrude","CAP_FACE",FACE,{"disambiguationData":[OSD([subQ0,sQuery(id+"F0.wireOp",EDGE,"E1.top"),sQuery(id+"F0.wireOp",EDGE,"E1.left"),sQuery(id+"F0.wireOp",EDGE,"E1.right")])],"isStart":true})]});}
            var Q34;
            {var subQ0=sQuery(id+"F0.wireOp",EDGE,"E0");Q34=makeQuery(id+"F6.opFillet","BLEND_EDGE",EDGE,{"blendedFrom":[makeQuery(id+"F5.boolean.opBoolean","INTERSECT",EDGE,{"derivedFrom":[makeQuery(id+"F3.boolean.opBoolean","MERGE",FACE,{"derivedFrom":[makeQuery(id+"F1.opExtrude","SWEPT_FACE",FACE,{"disambiguationData":[OSD([subQ0])]}),makeQuery(id+"F3.opExtrude","SWEPT_FACE",FACE,{"disambiguationData":[OSD([sQuery(id+"F2.wireOp",EDGE,"E4")])]})]}),makeQuery(id+"F5.opExtrude","SWEPT_FACE",FACE,{"disambiguationData":[OSD([sQuery(id+"F4.wireOp",EDGE,"E7.left")])]})]}),makeQuery(id+"F1.opExtrude","CAP_FACE",FACE,{"disambiguationData":[OSD([subQ0,sQuery(id+"F0.wireOp",EDGE,"E1.top"),sQuery(id+"F0.wireOp",EDGE,"E1.left"),sQuery(id+"F0.wireOp",EDGE,"E1.right")])],"isStart":true})],"blendedInto":[makeQuery(id+"F1.opExtrude","CAP_FACE",FACE,{"disambiguationData":[OSD([subQ0,sQuery(id+"F0.wireOp",EDGE,"E1.top"),sQuery(id+"F0.wireOp",EDGE,"E1.left"),sQuery(id+"F0.wireOp",EDGE,"E1.right")])],"isStart":true})]});}
            var Q35;
            Q35=makeQuery(id+"F12.boolean.opBoolean","COPY",EDGE,{"derivedFrom":makeQuery(id+"F12.opExtrude","CAP_EDGE",EDGE,{"disambiguationData":[OSD([sQuery(id+"F11.wireOp",EDGE,"E11")])],"isStart":true})});
            fillet(context, id + "F21", {"entities" : qUnion([Q0, Q1, Q2, Q3, Q4, Q5, Q6, Q7, Q8, Q9, Q10, Q11, Q12, Q13, Q14, Q15, Q16, Q17, Q18, Q19, Q20, Q21, Q22, Q23, Q24, Q25, Q26, Q27, Q28, Q29, Q30, Q31, Q32, Q33, Q34, Q35]), "radius" : .2 * mm, "allowEdgeOverflow" : false});
        }
    });
